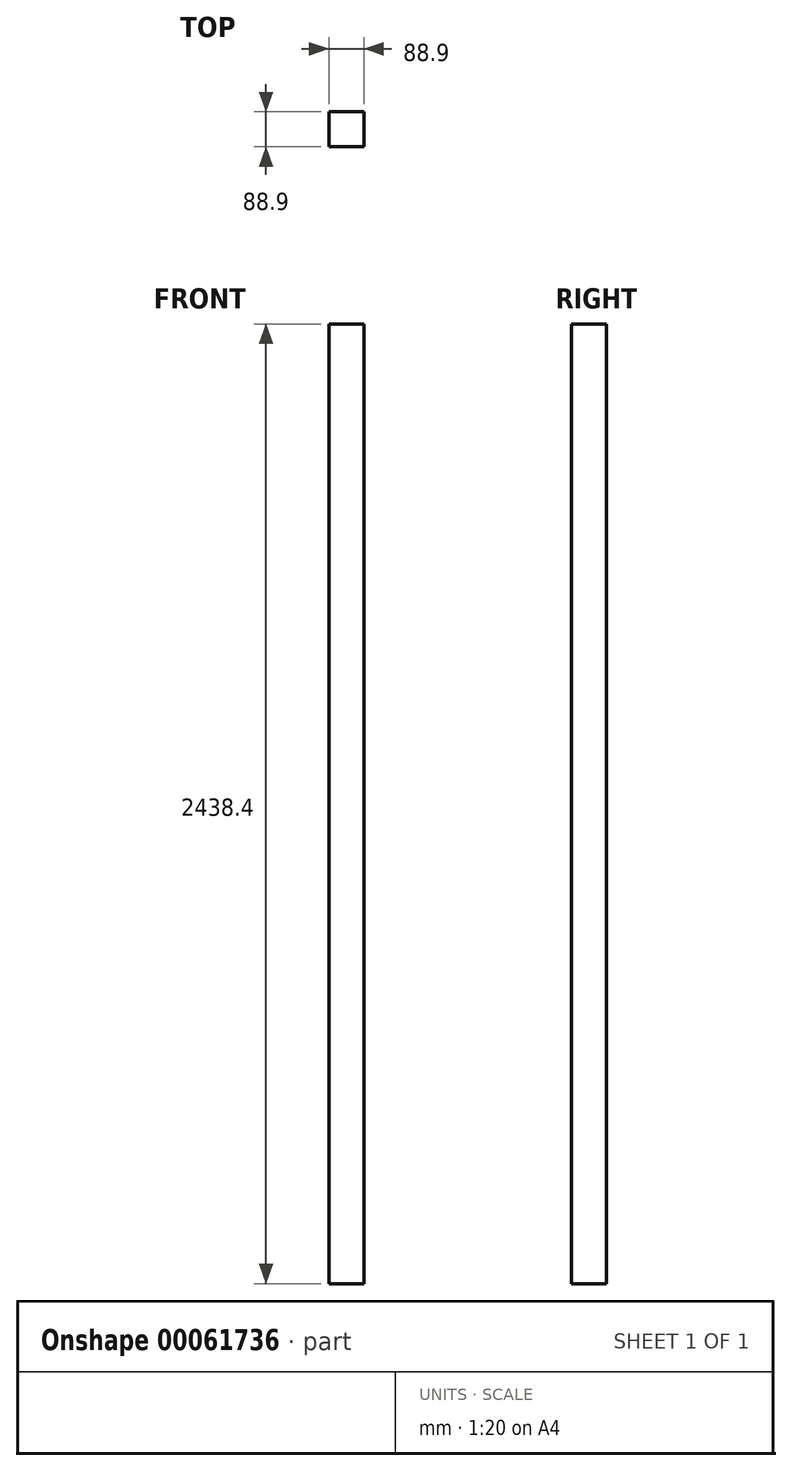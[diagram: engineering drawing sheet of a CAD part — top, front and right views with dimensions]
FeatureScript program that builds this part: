
annotation { "Feature Type Name" : "Feature", "Feature Type Description" : "" }
export const myFeature = defineFeature(function(context is Context, id is Id, definition is map)
    precondition{}
    {
        {
            var Q0;
            Q0=qCreatedBy(makeId("Top.planeOp"),FACE);
            var sketch = newSketch(context, id + "F0", { "sketchPlane" : qUnion([Q0])});
            skLineSegment(sketch, "E0", {"start": v(0, 0) * mm, "end": v(0, 88.9) * mm});
            skLineSegment(sketch, "E1", {"start": v(0, 88.9) * mm, "end": v(88.9, 88.9) * mm});
            skLineSegment(sketch, "E2", {"start": v(88.9, 88.9) * mm, "end": v(88.9, 0) * mm});
            skLineSegment(sketch, "E3", {"start": v(88.9, 0) * mm, "end": v(0, 0) * mm});
            skSolve(sketch);
        }
        {
            var Q0;
            Q0=makeQuery(id+"F0.imprint","IMPRINT",FACE,{"disambiguationData":[TD([[makeQuery(id+"F0.imprint","IMPRINT",EDGE,{"derivedFrom":sQuery(id+"F0.wireOp",EDGE,"E0")}),-1.0]])]});
            extrude(context, id + "F1", {"entities" : qUnion([Q0]), "depth" : 2438.4 * mm});
        }
    });
